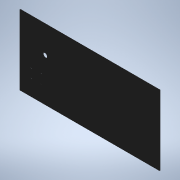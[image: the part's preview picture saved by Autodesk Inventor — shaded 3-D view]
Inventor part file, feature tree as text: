
AUTODESK INVENTOR PART (.ipt)
format: ipt  version: 2022 (Build 260153000, 153)  size: 112,640 bytes
history: native  units: mm
features: sketch x3, hole x2, other x1, extrude x1
ambient origin geometry x8: Origin, YZ Plane, XZ Plane, XY Plane, X Axis, Y Axis, Z Axis, Center Point
bodies: Body1 (feature_tree)
feature tree (7):
  other  "ソリッド1"
  extrude  "押し出し1"  Depth=360.0mm
  hole  "穴2"  [1 undecoded]
  hole  "穴3"  [1 undecoded]
  sketch  "スケッチ1"
  sketch  "スケッチ3"
  sketch  "スケッチ4"
note: 2 required parameter values undecoded (feature->parameter linkage not recoverable at this tier; creation-order binding heuristic only, values carry confidence <= 0.55)
